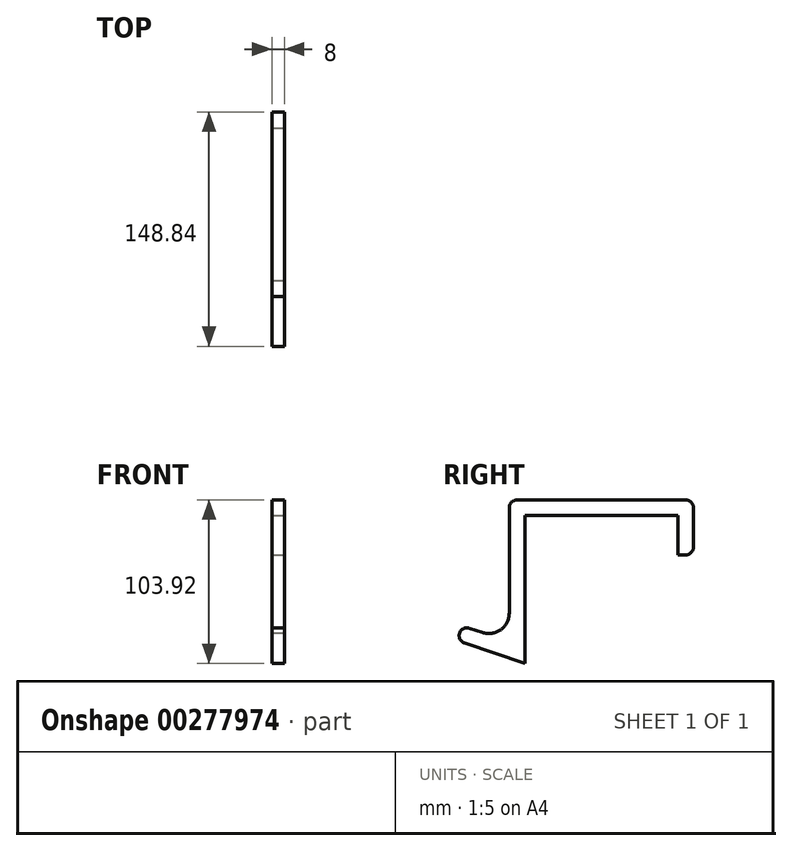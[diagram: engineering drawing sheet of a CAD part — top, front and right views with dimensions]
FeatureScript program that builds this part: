
annotation { "Feature Type Name" : "Feature", "Feature Type Description" : "" }
export const myFeature = defineFeature(function(context is Context, id is Id, definition is map)
    precondition{}
    {
        {
            var Q0;
            Q0=qCreatedBy(makeId("Right.planeOp"),FACE);
            var sketch = newSketch(context, id + "F0", { "sketchPlane" : qUnion([Q0])});
            skLineSegment(sketch, "E0", {"start": v(-1.6, 293.48) * mm, "end": v(115.4, 293.48) * mm});
            skLineSegment(sketch, "E1", {"start": v(115.4, 293.48) * mm, "end": v(115.4, 258.48) * mm});
            skLineSegment(sketch, "E2", {"start": v(115.4, 258.48) * mm, "end": v(105.4, 258.48) * mm});
            skLineSegment(sketch, "E3", {"start": v(105.4, 258.48) * mm, "end": v(105.4, 283.48) * mm});
            skLineSegment(sketch, "E4", {"start": v(105.4, 283.48) * mm, "end": v(8.4, 283.48) * mm});
            skLineSegment(sketch, "E5", {"start": v(-1.6, 293.48) * mm, "end": v(-1.6, 203.48) * mm});
            skLineSegment(sketch, "E6", {"start": v(8.4, 189.56) * mm, "end": v(-34.78, 204.09) * mm});
            skLineSegment(sketch, "E7", {"start": v(8.4, 283.48) * mm, "end": v(8.4, 189.56) * mm});
            skLineSegment(sketch, "E8.0", {"start": v(-1.6, 203.48) * mm, "end": v(-31.59, 213.57) * mm});
            skLineSegment(sketch, "E9", {"start": v(-31.59, 213.57) * mm, "end": v(-34.78, 204.09) * mm});
            skSolve(sketch);
        }
        {
            var Q0;
            Q0=qSketchRegion(id+"F0",true);
            extrude(context, id + "F1", {"entities" : qUnion([Q0]), "oppositeDirection" : true, "depth" : 8 * mm});
        }
        {
            var Q0;
            Q0=makeQuery(id+"F1.opExtrude","SWEPT_EDGE",EDGE,{"disambiguationData":[OSD([sQuery(id+"F0.wireOp",EDGE,"idZlt2Gv-Oq68-DV6A-WAP6-u2qqHt9ZvNW5"),sQuery(id+"F0.wireOp",EDGE,"E0")])]});
            var Q1;
            Q1=makeQuery(id+"F1.opExtrude","SWEPT_EDGE",EDGE,{"disambiguationData":[OSD([sQuery(id+"F0.wireOp",EDGE,"E0"),sQuery(id+"F0.wireOp",EDGE,"E1")])]});
            var Q2;
            Q2=makeQuery(id+"F1.opExtrude","SWEPT_EDGE",EDGE,{"disambiguationData":[OSD([sQuery(id+"F0.wireOp",EDGE,"E1"),sQuery(id+"F0.wireOp",EDGE,"E2")])]});
            fillet(context, id + "F2", {"entities" : qUnion([Q0, Q1, Q2]), "radius" : 5 * mm, "tangentPropagation" : true, "allowEdgeOverflow" : false});
        }
        {
            var Q0;
            Q0=makeQuery(id+"F1.opExtrude","SWEPT_EDGE",EDGE,{"disambiguationData":[OSD([sQuery(id+"F0.wireOp",EDGE,"E8.0"),sQuery(id+"F0.wireOp",EDGE,"E9")])]});
            var Q1;
            Q1=makeQuery(id+"F1.opExtrude","SWEPT_EDGE",EDGE,{"disambiguationData":[OSD([sQuery(id+"F0.wireOp",EDGE,"E6"),sQuery(id+"F0.wireOp",EDGE,"E9")])]});
            fillet(context, id + "F3", {"entities" : qUnion([Q0, Q1]), "radius" : 5 * mm, "tangentPropagation" : true, "allowEdgeOverflow" : false});
        }
        {
            var Q0;
            Q0=makeQuery(id+"F1.opExtrude","SWEPT_EDGE",EDGE,{"disambiguationData":[OSD([sQuery(id+"F0.wireOp",EDGE,"E5"),sQuery(id+"F0.wireOp",EDGE,"E8.0")])]});
            fillet(context, id + "F4", {"entities" : qUnion([Q0]), "radius" : 13 * mm, "tangentPropagation" : true, "allowEdgeOverflow" : false});
        }
    });
